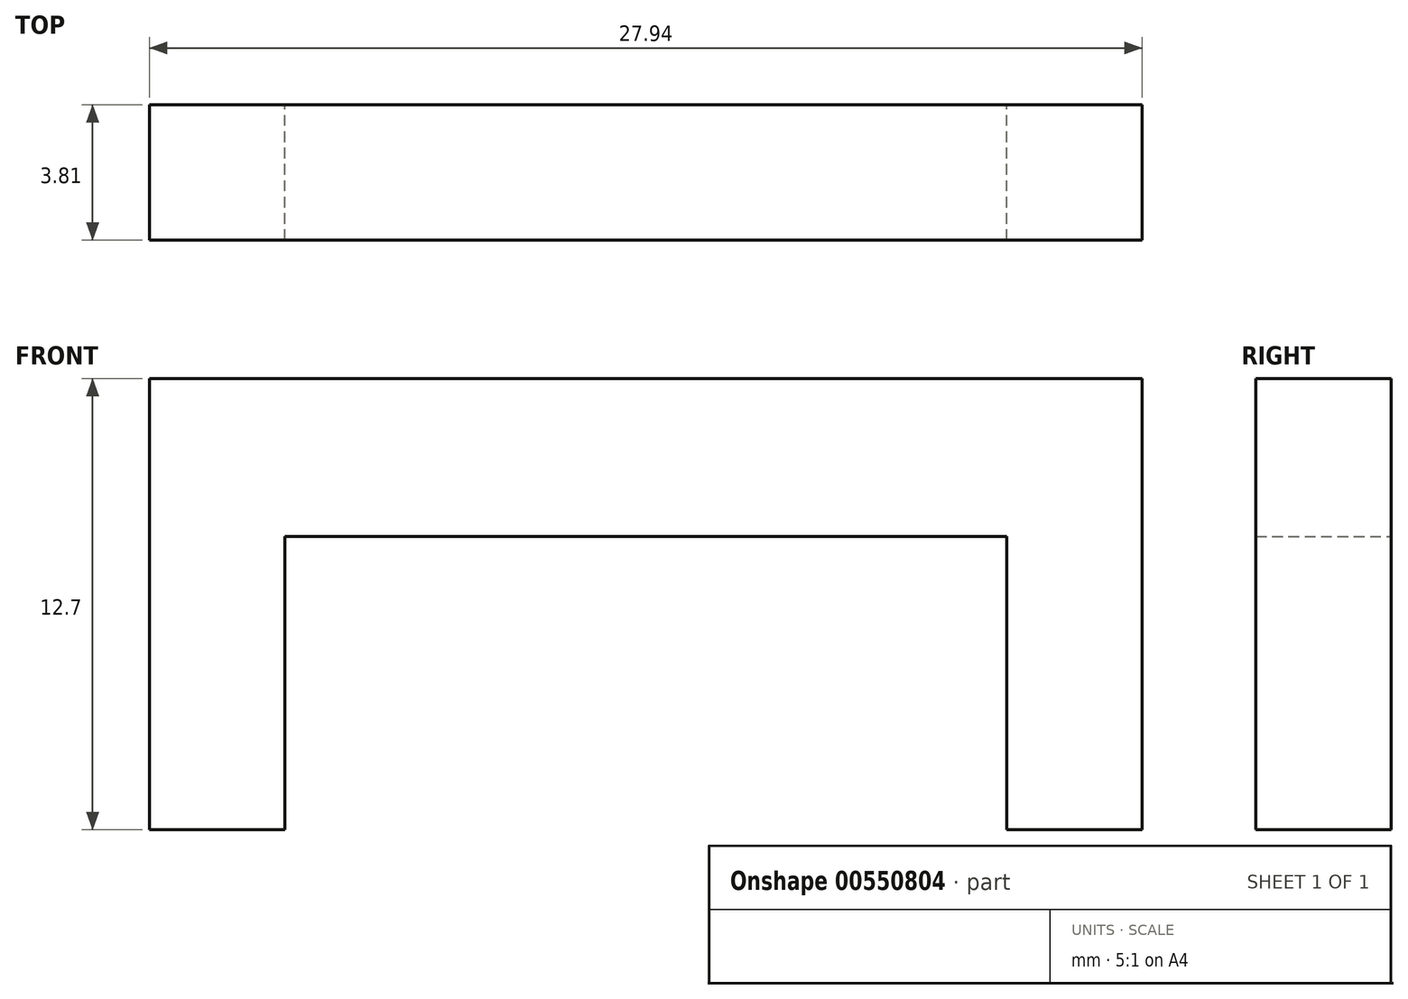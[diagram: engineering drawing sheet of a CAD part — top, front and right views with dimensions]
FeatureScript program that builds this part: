
annotation { "Feature Type Name" : "Feature", "Feature Type Description" : "" }
export const myFeature = defineFeature(function(context is Context, id is Id, definition is map)
    precondition{}
    {
        {
            var Q0;
            Q0=qCreatedBy(makeId("Front.planeOp"),FACE);
            var sketch = newSketch(context, id + "F0", { "sketchPlane" : qUnion([Q0])});
            skLineSegment(sketch, "E0", {"start": v(0, 0) * mm, "end": v(0, 12.7) * mm});
            skLineSegment(sketch, "E1", {"start": v(0, 12.7) * mm, "end": v(27.94, 12.7) * mm});
            skLineSegment(sketch, "E2", {"start": v(27.94, 12.7) * mm, "end": v(27.94, 0) * mm});
            skLineSegment(sketch, "E3", {"start": v(27.94, 0) * mm, "end": v(24.13, 0) * mm});
            skLineSegment(sketch, "E4", {"start": v(24.13, 0) * mm, "end": v(24.13, 8.26) * mm});
            skLineSegment(sketch, "E5", {"start": v(24.13, 8.26) * mm, "end": v(3.81, 8.26) * mm});
            skLineSegment(sketch, "E6", {"start": v(3.81, 8.26) * mm, "end": v(3.81, 0) * mm});
            skLineSegment(sketch, "E7", {"start": v(3.8, 0) * mm, "end": v(0, 0) * mm});
            skSolve(sketch);
        }
        {
            var Q0;
            Q0 = qSketchRegion(id + "F0", true);
            extrude(context, id + "F1", {"entities" : qUnion([Q0]), "depth" : 3.8 * mm, "offsetDistance" : 25.4 * mm});
        }
    });
